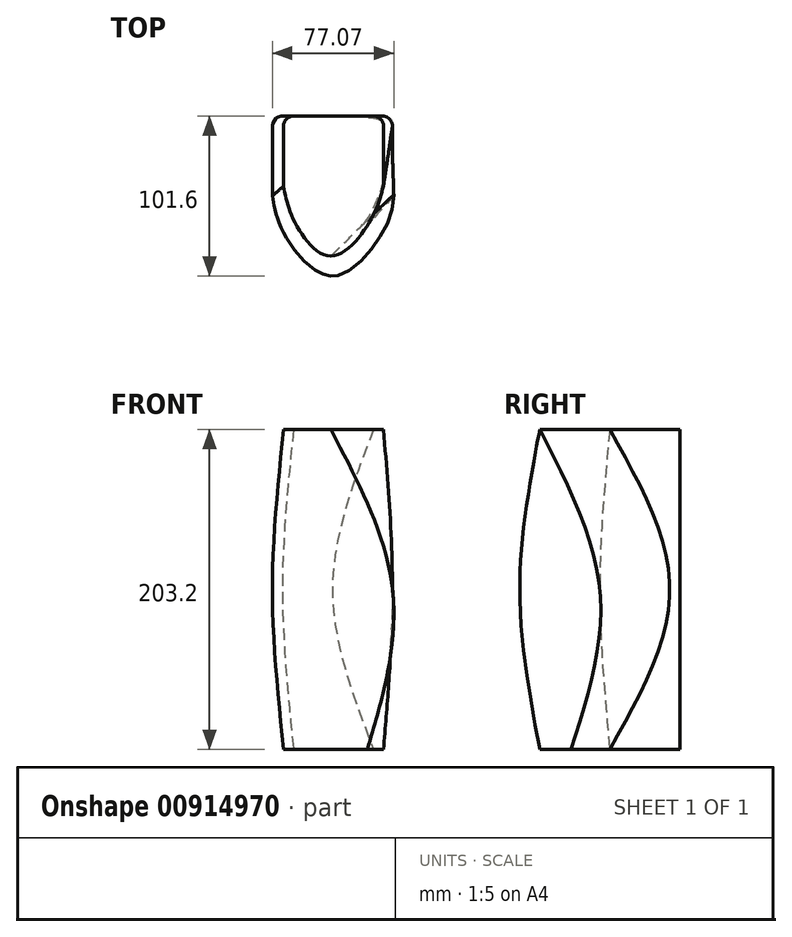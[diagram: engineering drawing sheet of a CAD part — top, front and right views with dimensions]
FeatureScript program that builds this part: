
annotation { "Feature Type Name" : "Feature", "Feature Type Description" : "" }
export const myFeature = defineFeature(function(context is Context, id is Id, definition is map)
    precondition{}
    {
        {
            var Q0;
            Q0=qCreatedBy(makeId("Top.planeOp"),FACE);
            cPlane(context, id + "F0", {"entities" : qUnion([Q0]), "cplaneType" : CPlaneType.OFFSET, "offset" : 101.6 * mm, "oppositeDirection" : true, "width" : 152.4 * mm, "height" : 152.4 * mm});
        }
        {
            var Q0;
            Q0=qCreatedBy(makeId("Top.planeOp"),FACE);
            cPlane(context, id + "F1", {"entities" : qUnion([Q0]), "cplaneType" : CPlaneType.OFFSET, "offset" : 101.6 * mm, "width" : 152.4 * mm, "height" : 152.4 * mm});
        }
        {
            var Q0;
            Q0=qCreatedBy(id+"F0.planeOp",FACE);
            var sketch = newSketch(context, id + "F2", { "sketchPlane" : qUnion([Q0])});
            skLineSegment(sketch, "E0", {"start": v(-23.42, 36.37) * mm, "end": v(27.38, 36.37) * mm});
            skLineSegment(sketch, "E1", {"start": v(-29.77, 36.37) * mm, "end": v(-29.77, -52.53) * mm, "construction": true});
            skLineSegment(sketch, "E2", {"start": v(-29.77, 30.02) * mm, "end": v(-29.77, -8.08) * mm});
            skLineSegment(sketch, "E3", {"start": v(33.73, 30.02) * mm, "end": v(33.73, -8.08) * mm});
            skLineSegment(sketch, "E4", {"start": v(-29.77, -52.53) * mm, "end": v(33.73, -52.53) * mm, "construction": true});
            skLineSegment(sketch, "E5", {"start": v(33.73, -52.53) * mm, "end": v(33.73, -8.08) * mm, "construction": true});
            skLineSegment(sketch, "E6", {"start": v(1.98, 36.37) * mm, "end": v(1.98, -52.53) * mm, "construction": true});
            skLineSegment(sketch, "E7", {"start": v(-29.77, -8.08) * mm, "end": v(33.73, -8.08) * mm, "construction": true});
            skLineSegment(sketch, "E8", {"start": v(33.73, 36.37) * mm, "end": v(-29.77, -52.53) * mm, "construction": true});
            skLineSegment(sketch, "E9", {"start": v(-29.77, 36.37) * mm, "end": v(33.73, -52.53) * mm, "construction": true});
            skLineSegment(sketch, "E10", {"start": v(-29.77, 14.15) * mm, "end": v(33.73, 14.15) * mm, "construction": true});
            skLineSegment(sketch, "E11", {"start": v(33.73, -30.3) * mm, "end": v(-29.77, -30.3) * mm, "construction": true});
            skFitSpline(sketch, "E12", {"points": [v(-29.77, -8.08) * mm, v(-23, -30.3) * mm, v(0, -52.53) * mm, v(24.96, -30.3) * mm, v(33.73, -8.08) * mm], "startDerivative": vector(17.04, -90.52) * mm, "endDerivative": vector(25.44, 89.06) * mm});
            skPoint(sketch, "E13.visualSharp", {"position": v(-29.77, 36.37) * mm});
            skArc(sketch, "E13.filletArc", {"start": v(-23.42, 36.37) * mm, "mid": v(-27.9, 34.51) * mm, "end": v(-29.77, 30.02) * mm});
            skPoint(sketch, "E14.visualSharp", {"position": v(33.73, 36.37) * mm});
            skArc(sketch, "E14.filletArc", {"start": v(33.73, 30.02) * mm, "mid": v(31.87, 34.51) * mm, "end": v(27.38, 36.37) * mm});
            skSolve(sketch);
        }
        {
            var Q0;
            Q0=qCreatedBy(makeId("Top.planeOp"),FACE);
            var sketch = newSketch(context, id + "F3", { "sketchPlane" : qUnion([Q0])});
            skLineSegment(sketch, "E15", {"start": v(-36.79, 36.37) * mm, "end": v(39.41, 36.37) * mm, "construction": true});
            skLineSegment(sketch, "E16", {"start": v(-36.79, 36.37) * mm, "end": v(-36.79, -65.23) * mm, "construction": true});
            skLineSegment(sketch, "E17", {"start": v(-36.79, -65.23) * mm, "end": v(39.41, -65.23) * mm, "construction": true});
            skLineSegment(sketch, "E18", {"start": v(39.41, 36.37) * mm, "end": v(39.41, -65.23) * mm, "construction": true});
            skLineSegment(sketch, "E19", {"start": v(-36.79, -14.43) * mm, "end": v(39.41, -14.43) * mm, "construction": true});
            skLineSegment(sketch, "E20", {"start": v(39.41, -14.43) * mm, "end": v(1.31, 36.37) * mm, "construction": true});
            skLineSegment(sketch, "E21", {"start": v(1.31, 36.37) * mm, "end": v(-36.79, -14.43) * mm, "construction": true});
            skLineSegment(sketch, "E22", {"start": v(-36.79, -14.43) * mm, "end": v(1.31, -65.23) * mm, "construction": true});
            skLineSegment(sketch, "E23", {"start": v(1.31, -65.23) * mm, "end": v(39.41, -14.43) * mm, "construction": true});
            skLineSegment(sketch, "E24", {"start": v(-36.79, 30.02) * mm, "end": v(-36.79, -14.43) * mm});
            skLineSegment(sketch, "E25", {"start": v(-30.44, 36.37) * mm, "end": v(33.06, 36.37) * mm});
            skLineSegment(sketch, "E26", {"start": v(39.41, 30.02) * mm, "end": v(39.41, -14.43) * mm});
            skLineSegment(sketch, "E27", {"start": v(-36.79, 10.97) * mm, "end": v(39.41, 10.97) * mm, "construction": true});
            skLineSegment(sketch, "E28", {"start": v(39.41, -14.43) * mm, "end": v(-36.79, -14.43) * mm, "construction": true});
            skLineSegment(sketch, "E29", {"start": v(-36.79, -41.86) * mm, "end": v(39.41, -41.86) * mm, "construction": true});
            skFitSpline(sketch, "E30", {"points": [v(-36.79, -14.43) * mm, v(-27.3, -41.86) * mm, v(1.31, -65.23) * mm, v(30.37, -41.86) * mm, v(39.41, -14.43) * mm], "startDerivative": vector(13.8, -114.05) * mm, "endDerivative": vector(-6.36, 116.15) * mm});
            skPoint(sketch, "E31.visualSharp", {"position": v(-36.79, 36.37) * mm});
            skArc(sketch, "E31.filletArc", {"start": v(-30.44, 36.37) * mm, "mid": v(-34.93, 34.51) * mm, "end": v(-36.79, 30.02) * mm});
            skPoint(sketch, "E32.visualSharp", {"position": v(39.41, 36.37) * mm});
            skArc(sketch, "E32.filletArc", {"start": v(39.41, 30.02) * mm, "mid": v(37.55, 34.51) * mm, "end": v(33.06, 36.37) * mm});
            skSolve(sketch);
        }
        {
            var Q0;
            Q0=qCreatedBy(id+"F1.planeOp",FACE);
            var sketch = newSketch(context, id + "F4", { "sketchPlane" : qUnion([Q0])});
            skLineSegment(sketch, "E33", {"start": v(-29.77, 36.37) * mm, "end": v(33.73, 36.37) * mm, "construction": true});
            skLineSegment(sketch, "E34", {"start": v(-29.77, 36.37) * mm, "end": v(-29.77, -52.53) * mm, "construction": true});
            skLineSegment(sketch, "E35", {"start": v(-29.77, -52.53) * mm, "end": v(33.73, -52.53) * mm});
            skLineSegment(sketch, "E36", {"start": v(33.73, 36.37) * mm, "end": v(33.73, -52.53) * mm, "construction": true});
            skLineSegment(sketch, "E37", {"start": v(-29.77, 14.11) * mm, "end": v(33.73, 14.11) * mm, "construction": true});
            skLineSegment(sketch, "E38", {"start": v(-29.77, -8.08) * mm, "end": v(33.73, -8.08) * mm, "construction": true});
            skLineSegment(sketch, "E39", {"start": v(-29.77, -30.05) * mm, "end": v(33.73, -30.05) * mm, "construction": true});
            skLineSegment(sketch, "E40", {"start": v(1.98, 36.37) * mm, "end": v(1.98, -52.53) * mm, "construction": true});
            skLineSegment(sketch, "E41", {"start": v(33.3, 37.23) * mm, "end": v(-29.77, -52.53) * mm, "construction": true});
            skLineSegment(sketch, "E42", {"start": v(-29.77, 36.37) * mm, "end": v(33.73, -52.53) * mm, "construction": true});
            skLineSegment(sketch, "E43", {"start": v(-23.42, 36.37) * mm, "end": v(27.38, 36.37) * mm});
            skLineSegment(sketch, "E44", {"start": v(33.73, 30.02) * mm, "end": v(33.73, -8.08) * mm});
            skLineSegment(sketch, "E45", {"start": v(-29.77, 30.02) * mm, "end": v(-29.77, -8.08) * mm});
            skFitSpline(sketch, "E46", {"points": [v(-29.77, -8.08) * mm, v(-22.93, -30.32) * mm, v(0, -52.53) * mm, v(25.3, -30.05) * mm, v(33.73, -8.08) * mm], "startDerivative": vector(17.51, -90.47) * mm, "endDerivative": vector(23.75, 88.46) * mm});
            skPoint(sketch, "E47.visualSharp", {"position": v(-29.77, 36.37) * mm});
            skArc(sketch, "E47.filletArc", {"start": v(-23.42, 36.37) * mm, "mid": v(-27.9, 34.51) * mm, "end": v(-29.77, 30.02) * mm});
            skPoint(sketch, "E48.visualSharp", {"position": v(33.73, 36.37) * mm});
            skArc(sketch, "E48.filletArc", {"start": v(33.73, 30.02) * mm, "mid": v(31.87, 34.51) * mm, "end": v(27.38, 36.37) * mm});
            skSolve(sketch);
        }
        {
            var Q0;
            Q0=makeQuery(id+"F4.imprint","IMPRINT",FACE,{"disambiguationData":[TD([[makeQuery(id+"F4.imprint","IMPRINT",EDGE,{"derivedFrom":sQuery(id+"F4.wireOp",EDGE,"E43")}),-1.0]])]});
            var Q1;
            Q1=makeQuery(id+"F3.imprint","IMPRINT",FACE,{"disambiguationData":[TD([[makeQuery(id+"F3.imprint","IMPRINT",EDGE,{"derivedFrom":sQuery(id+"F3.wireOp",EDGE,"E24")}),1.0]])]});
            var Q2;
            Q2=makeQuery(id+"F2.imprint","IMPRINT",FACE,{"disambiguationData":[TD([[makeQuery(id+"F2.imprint","IMPRINT",EDGE,{"derivedFrom":sQuery(id+"F2.wireOp",EDGE,"E0")}),-1.0]])]});
            var Q3;
            Q3=sQuery(id+"F3.wireOp",VERTEX,"E22.end");
            var Q4;
            Q4=sQuery(id+"F2.wireOp",VERTEX,"E12.2.internal");
            var Q5;
            Q5=sQuery(id+"F4.wireOp",VERTEX,"E46.2.internal");
            loft(context, id + "F5", {"sheetProfilesArray" : [{ "sheetProfileEntities" : qUnion([Q0]) }, { "sheetProfileEntities" : qUnion([Q1]) }, { "sheetProfileEntities" : qUnion([Q2]) }], "matchConnections" : true, "connections" : [{ "connectionEntities" : qUnion([Q3, Q4, Q5]), "connectionEdgeQueries" : qUnion([]), "connectionEdgeParameters" : [] }]});
        }
    });
